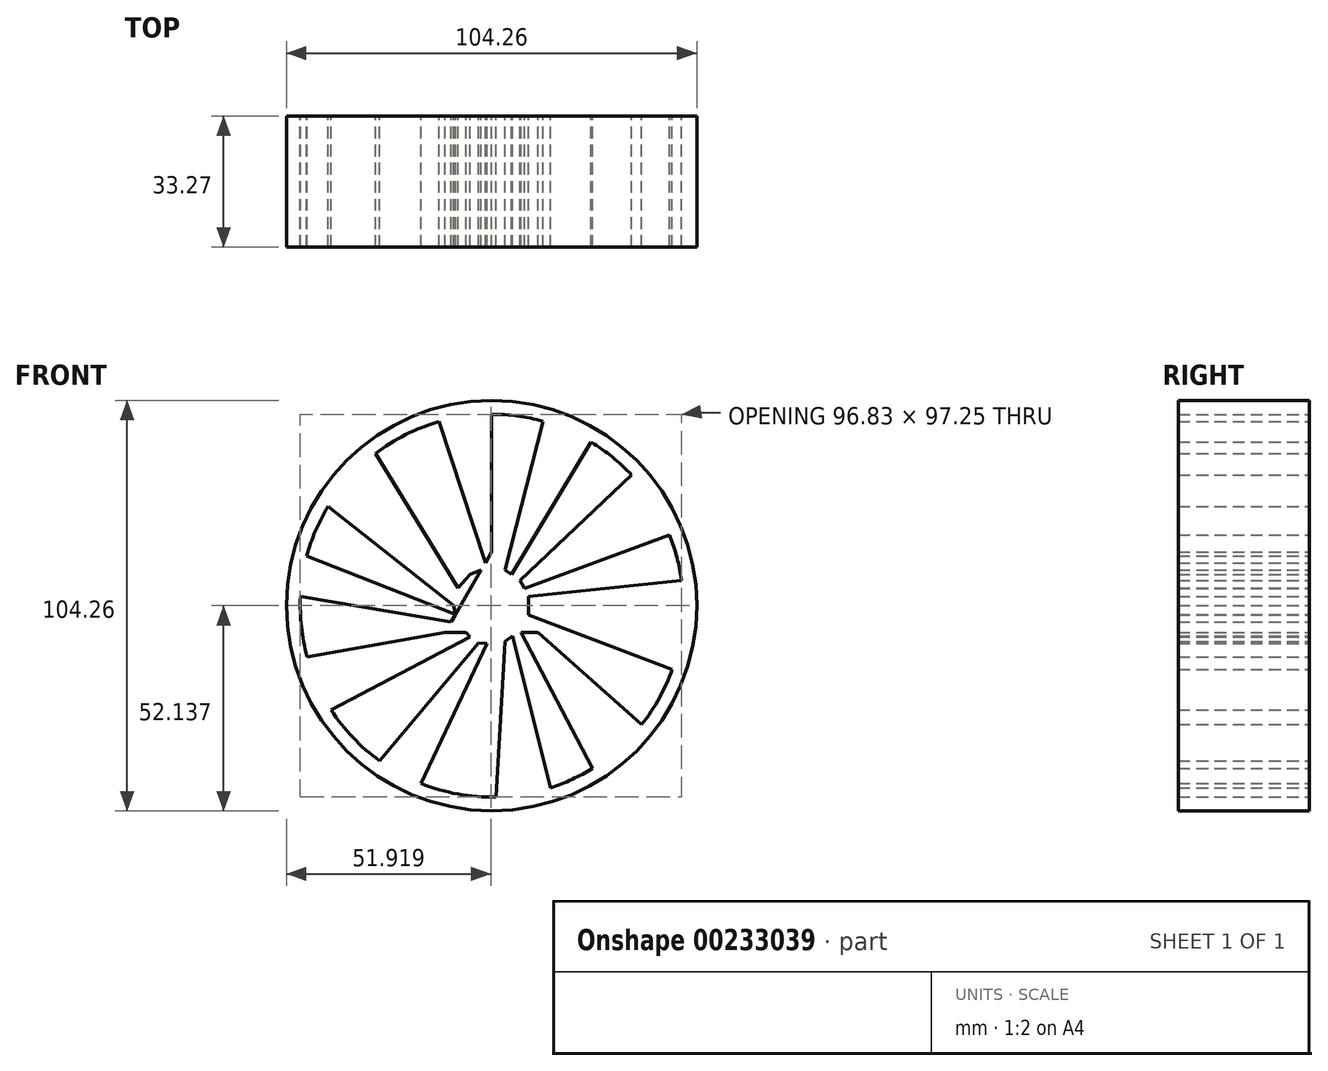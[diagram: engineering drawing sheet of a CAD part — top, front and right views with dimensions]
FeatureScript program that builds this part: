
annotation { "Feature Type Name" : "Feature", "Feature Type Description" : "" }
export const myFeature = defineFeature(function(context is Context, id is Id, definition is map)
    precondition{}
    {
        {
            var Q0;
            Q0=qCreatedBy(makeId("Front.planeOp"),FACE);
            var sketch = newSketch(context, id + "F0", { "sketchPlane" : qUnion([Q0])});
            skArc(sketch, "E0", {"start": v(-13.43, 46.74) * mm, "mid": v(-21.87, 43.43) * mm, "end": v(-29.55, 38.62) * mm});
            skCircle(sketch, "E1.cCircle", {"center": v(0, 0) * mm, "radius": 9.39 * mm, "construction": true});
            skLineSegment(sketch, "E1.0", {"start": v(9.39, 2.31) * mm, "end": v(9.39, -2.31) * mm});
            skLineSegment(sketch, "E1.1", {"start": v(9.39, -2.31) * mm, "end": v(7.24, -6.41) * mm});
            skLineSegment(sketch, "E1.2", {"start": v(7.24, -6.41) * mm, "end": v(3.43, -9.04) * mm});
            skLineSegment(sketch, "E1.3", {"start": v(3.43, -9.04) * mm, "end": v(-1.17, -9.6) * mm});
            skLineSegment(sketch, "E1.4", {"start": v(-1.17, -9.6) * mm, "end": v(-5.5, -7.96) * mm});
            skLineSegment(sketch, "E1.5", {"start": v(-5.5, -7.96) * mm, "end": v(-8.56, -4.5) * mm});
            skLineSegment(sketch, "E1.6", {"start": v(-8.56, -4.5) * mm, "end": v(-9.67, 0) * mm});
            skLineSegment(sketch, "E1.7", {"start": v(-9.67, 0) * mm, "end": v(-8.56, 4.5) * mm});
            skLineSegment(sketch, "E1.8", {"start": v(-8.56, 4.5) * mm, "end": v(-5.5, 7.96) * mm});
            skLineSegment(sketch, "E1.9", {"start": v(-5.5, 7.96) * mm, "end": v(-1.17, 9.6) * mm});
            skLineSegment(sketch, "E1.10", {"start": v(-1.17, 9.6) * mm, "end": v(3.43, 9.04) * mm});
            skLineSegment(sketch, "E1.11", {"start": v(3.43, 9.04) * mm, "end": v(7.24, 6.41) * mm});
            skLineSegment(sketch, "E1.12", {"start": v(7.24, 6.41) * mm, "end": v(9.39, 2.31) * mm});
            skPoint(sketch, "E1.0.midPoint", {"position": v(9.39, 0) * mm});
            skLineSegment(sketch, "E2", {"start": v(-1.17, 9.6) * mm, "end": v(-13.43, 46.74) * mm});
            skLineSegment(sketch, "E3", {"start": v(3.43, 9.04) * mm, "end": v(13.04, 46.85) * mm});
            skLineSegment(sketch, "E4", {"start": v(7.24, 6.41) * mm, "end": v(35.54, 33.19) * mm});
            skLineSegment(sketch, "E5", {"start": v(9.39, 2.31) * mm, "end": v(48.2, 6.41) * mm});
            skLineSegment(sketch, "E6", {"start": v(9.39, -2.31) * mm, "end": v(45.87, -16.15) * mm});
            skLineSegment(sketch, "E7", {"start": v(7.24, -6.41) * mm, "end": v(25.58, -41.36) * mm});
            skLineSegment(sketch, "E8", {"start": v(3.43, -9.04) * mm, "end": v(1.13, -48.62) * mm});
            skPoint(sketch, "E8.endSnap0", {"position": v(1.13, -9.32) * mm});
            skLineSegment(sketch, "E9", {"start": v(-1.17, -9.6) * mm, "end": v(-17.91, -45.21) * mm});
            skLineSegment(sketch, "E10", {"start": v(-5.5, -7.96) * mm, "end": v(-40.79, -26.48) * mm});
            skLineSegment(sketch, "E11", {"start": v(-8.56, -4.5) * mm, "end": v(-48.57, 2.31) * mm});
            skLineSegment(sketch, "E12", {"start": v(-9.67, 0) * mm, "end": v(-41.59, 25.2) * mm});
            skLineSegment(sketch, "E13", {"start": v(-8.56, 4.5) * mm, "end": v(-29.55, 38.62) * mm});
            skCircle(sketch, "E14.cCircle", {"center": v(0, 0) * mm, "radius": 6.83 * mm, "construction": true});
            skLineSegment(sketch, "E14.0", {"start": v(11.83, -6.83) * mm, "end": v(-11.83, -6.83) * mm});
            skLineSegment(sketch, "E14.1", {"start": v(-11.83, -6.83) * mm, "end": v(0, 13.66) * mm});
            skLineSegment(sketch, "E14.2", {"start": v(0, 13.66) * mm, "end": v(11.83, -6.83) * mm});
            skPoint(sketch, "E14.0.midPoint", {"position": v(0, -6.83) * mm});
            skLineSegment(sketch, "E15", {"start": v(0, 13.66) * mm, "end": v(0, 48.63) * mm});
            skLineSegment(sketch, "E16", {"start": v(11.83, -6.83) * mm, "end": v(38.12, -30.2) * mm});
            skLineSegment(sketch, "E17", {"start": v(-11.83, -6.83) * mm, "end": v(-46.87, -12.97) * mm});
            skLineSegment(sketch, "E18", {"start": v(8.31, 4.36) * mm, "end": v(45.21, 17.91) * mm});
            skLineSegment(sketch, "E19", {"start": v(4.18, 6.41) * mm, "end": v(25.29, 41.54) * mm});
            skLineSegment(sketch, "E20", {"start": v(-1.17, -9.6) * mm, "end": v(-3.33, -9.47) * mm});
            skPoint(sketch, "E20.endSnap0", {"position": v(-3.33, -8.78) * mm});
            skLineSegment(sketch, "E21", {"start": v(-3.33, -9.47) * mm, "end": v(-28.53, -39.38) * mm});
            skLineSegment(sketch, "E22", {"start": v(5.33, -7.73) * mm, "end": v(15.36, -47.8) * mm});
            skLineSegment(sketch, "E23", {"start": v(-9.12, -2.25) * mm, "end": v(-46.97, 12.6) * mm});
            skCircle(sketch, "E24", {"center": v(0, 0) * mm, "radius": 52.13 * mm});
            skArc(sketch, "E25.trimOffspring", {"start": v(-41.59, 25.2) * mm, "mid": v(-44.73, 19.1) * mm, "end": v(-46.97, 12.6) * mm});
            skArc(sketch, "E26.trimOffspring", {"start": v(-48.57, 2.31) * mm, "mid": v(-48.33, -5.4) * mm, "end": v(-46.87, -12.97) * mm});
            skArc(sketch, "E27.trimOffspring", {"start": v(-40.79, -26.48) * mm, "mid": v(-35.25, -33.5) * mm, "end": v(-28.53, -39.38) * mm});
            skArc(sketch, "E28.trimOffspring", {"start": v(-17.91, -45.21) * mm, "mid": v(-8.56, -47.87) * mm, "end": v(1.13, -48.62) * mm});
            skArc(sketch, "E29.trimOffspring", {"start": v(14.98, -46.27) * mm, "mid": v(20.43, -44.13) * mm, "end": v(25.58, -41.36) * mm});
            skArc(sketch, "E30.trimOffspring", {"start": v(38.12, -30.2) * mm, "mid": v(42.58, -23.5) * mm, "end": v(45.87, -16.15) * mm});
            skArc(sketch, "E31.trimOffspring", {"start": v(48.2, 6.41) * mm, "mid": v(47.06, 12.25) * mm, "end": v(45.21, 17.91) * mm});
            skArc(sketch, "E32.trimOffspring", {"start": v(35.54, 33.19) * mm, "mid": v(30.7, 37.71) * mm, "end": v(25.29, 41.54) * mm});
            skArc(sketch, "E33.trimOffspring", {"start": v(13.04, 46.85) * mm, "mid": v(6.58, 48.18) * mm, "end": v(0, 48.63) * mm});
            skSolve(sketch);
        }
        {
            var Q0;
            Q0 = qSketchRegion(id + "F0", true);
            extrude(context, id + "F1", {"entities" : qUnion([Q0]), "depth" : 25.4 * mm});
        }
        {
            var Q0;
            Q0 = qSketchRegion(id + "F0", true);
            var Q1;
            {var subQ4=sQuery(id+"F0.wireOp",EDGE,"E1.7");Q1=makeQuery(id+"F0.imprint","IMPRINT",FACE,{"disambiguationData":[TD([[makeQuery(id+"F0.imprint","IMPRINT",EDGE,{"derivedFrom":subQ4}),-1.0]])]});}
            extrude(context, id + "F2", {"entities" : qUnion([Q0, Q1]), "operationType" : NewBodyOperationType.ADD, "depth" : 33.27 * mm});
        }
    });
